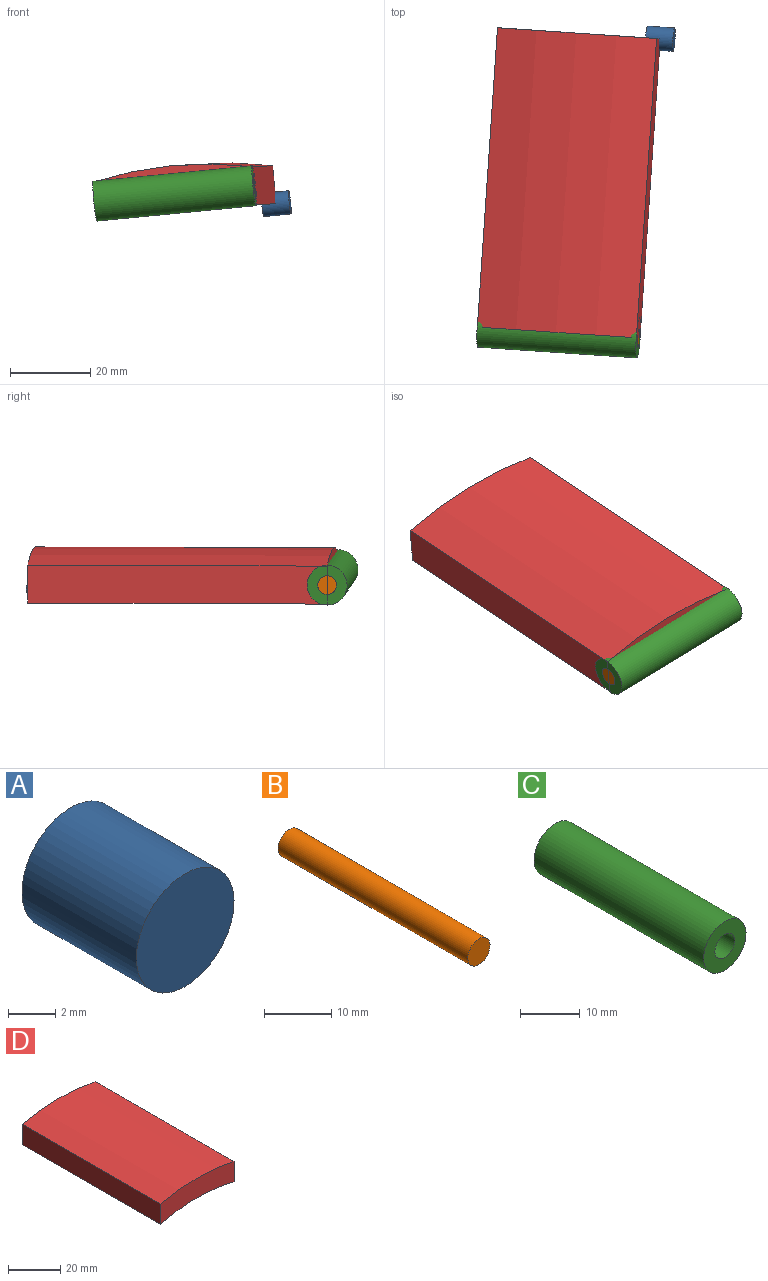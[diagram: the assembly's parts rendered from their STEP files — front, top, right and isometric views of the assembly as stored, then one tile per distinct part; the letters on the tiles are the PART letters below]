
ASSEMBLY  parts=4 mates=3
PART A: 3 faces, bbox 5.8x6.8x5.8 mm
  f0: cylinder r=2.92mm len=6.85mm, axis (0,1,0), area 125.6mm2, adj f1,f2
  f1: plane 5.84x5.84mm, normal (0,-1,0), area 26.8mm2, adj f0
  f2: plane 5.84x5.84mm, normal (0,1,0), area 26.8mm2, adj f0
PART B: 3 faces, bbox 4.7x40x4.7 mm
  f0: cylinder r=2.34mm len=40.01mm, axis (0,1,0), area 588.6mm2, adj f1,f2
  f1: plane 4.68x4.68mm, normal (0,-1,0), area 17.2mm2, adj f0
  f2: plane 4.68x4.68mm, normal (0,1,0), area 17.2mm2, adj f0
PART C: 4 faces, bbox 10x40x10 mm
  f0: cylinder r=2.34mm len=40.01mm, axis (0,1,0), area 587.4mm2, adj f2,f3
  f1: cylinder r=5mm len=40.01mm, axis (0,1,0), area 1257.7mm2, adj f2,f3
  f2: plane 10.01x10.01mm, normal (0,-1,0), area 61.5mm2, adj f0,f1
  f3: plane 10.01x10.01mm, normal (0,1,0), area 61.5mm2, adj f0,f1
PART D: 6 faces, bbox 40x74.9x11.7 mm
  f0: plane 74.93x9.53mm, normal (1,0,0), area 713.9mm2, adj f1,f3,f4,f5
  f1: cylinder r=92.06mm len=74.93mm, axis (0,1,0), area 3021.3mm2, adj f0,f2,f4,f5
  f2: plane 74.93x9.53mm, normal (-1,0,0), area 713.9mm2, adj f1,f3,f4,f5
  f3: cylinder r=79.98mm len=74.93mm, axis (0,1,0), area 3029.4mm2, adj f0,f2,f4,f5
  f4: plane 40x11.73mm, normal (0,-1,0), area 371.9mm2, adj f0,f1,f2,f3
  f5: plane 40x11.73mm, normal (0,1,0), area 371.9mm2, adj f0,f1,f2,f3
PLACE A rot(axis=(0.05,-0.05,-1),94deg) t=(22.24,-74.48,-35.02)mm
PLACE B rot(axis=(-0.05,-0.05,1),86.3deg) t=(-26.48,-107.34,-6.45)mm
PLACE C rot(axis=(-0.05,-0.05,1),86.3deg) t=(-21.5,-74.14,-34.64)mm
PLACE D rot(axis=(-0.05,0,1),176.1deg) t=(-5.84,-108.72,-12.55)mm
MATE revolute C.f0 <-> B.f0  axis (-0.99,0.07,-0.1) through (-6.62,-108.69,-4.52)mm
MATE fastened D.f2 <-> C.f0  axis (0.99,-0.07,0.1) through (13.25,-110.04,-2.6)mm
MATE fastened A.f0 <-> D.f2  axis (0.99,-0.07,0.1) through (18.75,-35.29,-7.09)mm
